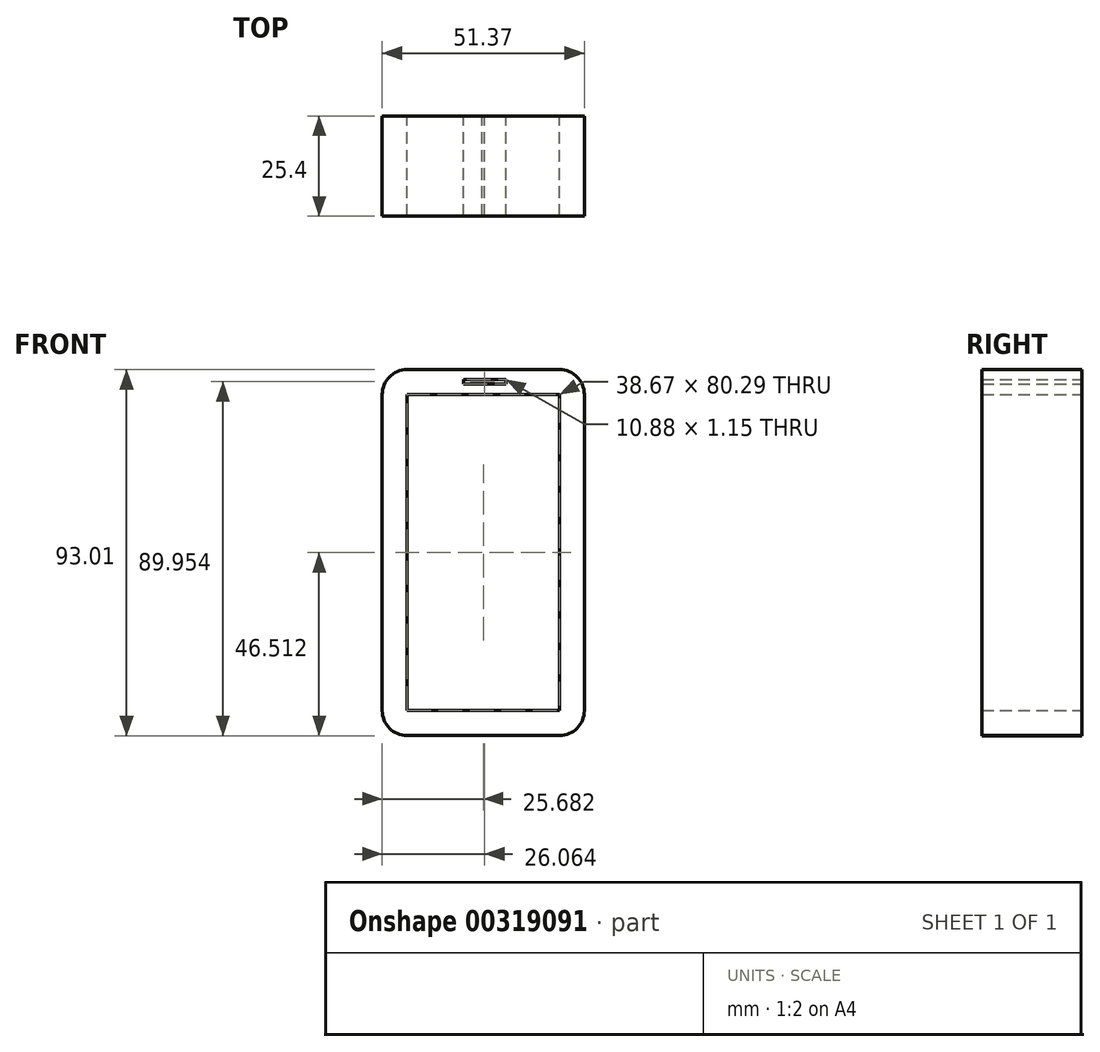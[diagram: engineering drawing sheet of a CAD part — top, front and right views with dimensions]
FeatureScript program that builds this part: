
annotation { "Feature Type Name" : "Feature", "Feature Type Description" : "" }
export const myFeature = defineFeature(function(context is Context, id is Id, definition is map)
    precondition{}
    {
        {
            var Q0;
            Q0=qCreatedBy(makeId("Front.planeOp"),FACE);
            var sketch = newSketch(context, id + "F0", { "sketchPlane" : qUnion([Q0])});
            skLineSegment(sketch, "E0.bottom", {"start": v(-35.85, 41.82) * mm, "end": v(2.82, 41.82) * mm});
            skLineSegment(sketch, "E0.top", {"start": v(-35.85, -51.18) * mm, "end": v(2.82, -51.18) * mm});
            skLineSegment(sketch, "E0.left", {"start": v(-42.2, 35.47) * mm, "end": v(-42.2, -44.83) * mm});
            skLineSegment(sketch, "E0.right", {"start": v(9.17, 35.47) * mm, "end": v(9.17, -44.83) * mm});
            skPoint(sketch, "E1.visualSharp", {"position": v(-42.2, 41.82) * mm});
            skArc(sketch, "E1.filletArc", {"start": v(-35.85, 41.82) * mm, "mid": v(-40.34, 39.96) * mm, "end": v(-42.2, 35.47) * mm});
            skPoint(sketch, "E2.visualSharp", {"position": v(9.17, 41.82) * mm});
            skArc(sketch, "E2.filletArc", {"start": v(9.17, 35.47) * mm, "mid": v(7.3, 39.96) * mm, "end": v(2.82, 41.82) * mm});
            skPoint(sketch, "E3.visualSharp", {"position": v(-42.2, -51.18) * mm});
            skArc(sketch, "E3.filletArc", {"start": v(-42.2, -44.83) * mm, "mid": v(-40.34, -49.32) * mm, "end": v(-35.85, -51.18) * mm});
            skPoint(sketch, "E4.visualSharp", {"position": v(9.17, -51.18) * mm});
            skArc(sketch, "E4.filletArc", {"start": v(2.82, -51.18) * mm, "mid": v(7.3, -49.32) * mm, "end": v(9.17, -44.83) * mm});
            skLineSegment(sketch, "E5.bottom", {"start": v(-35.85, 35.47) * mm, "end": v(2.82, 35.47) * mm});
            skLineSegment(sketch, "E5.top", {"start": v(-35.85, -44.83) * mm, "end": v(2.82, -44.83) * mm});
            skLineSegment(sketch, "E5.left", {"start": v(-35.85, 35.47) * mm, "end": v(-35.85, -44.83) * mm});
            skLineSegment(sketch, "E5.right", {"start": v(2.82, 35.47) * mm, "end": v(2.82, -44.83) * mm});
            skCircle(sketch, "E6", {"center": v(-16.52, -47.93) * mm, "radius": 3.26 * mm});
            skPoint(sketch, "E6.centerSnap0", {"position": v(-16.52, -44.83) * mm});
            skLineSegment(sketch, "E7.bottom", {"start": v(-21.58, 39.34) * mm, "end": v(-10.7, 39.34) * mm});
            skLineSegment(sketch, "E7.top", {"start": v(-21.58, 38.2) * mm, "end": v(-10.7, 38.2) * mm});
            skLineSegment(sketch, "E7.left", {"start": v(-21.58, 39.34) * mm, "end": v(-21.58, 38.2) * mm});
            skLineSegment(sketch, "E7.right", {"start": v(-10.7, 39.34) * mm, "end": v(-10.7, 38.2) * mm});
            skSolve(sketch);
        }
        {
            var Q0;
            Q0 = qSketchRegion(id + "F0", true);
            extrude(context, id + "F1", {"entities" : qUnion([Q0]), "depth" : 25.4 * mm});
        }
    });
